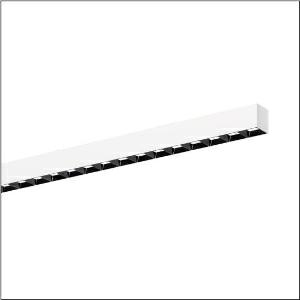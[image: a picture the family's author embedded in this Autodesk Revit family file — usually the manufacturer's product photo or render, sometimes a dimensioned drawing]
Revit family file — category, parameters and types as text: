
# Revit family: silica_r__21_51mx22da34wb_da43
name_source: partatom
category: Lighting Fixtures
units: mm (PartAtom-declared; Revit-internal decimal feet)

## family parameters
Cut with Voids When Loaded = No
Host = Face
Light Source = No
Part Type = Normal
Room Calculation Point = No
Round Connector Dimension = Use Diameter
Shared = No

## types (1)
- --- (1 x LED, 4320 lm, 27.4 W, 3000K)
    Apparent Load = 27 VA
    CIE Flux Codes = 86 100 100 100 100
    Color Rendering = 80
    Color Temperature = 3000K
    Default Elevation = 1800 mm
    Description = Silica® 21, office luminaire, primary light control with darklight reflector, of PMMA, black, CAT 2 (L<= 3000cd/m²), light emission: direct distribution, primary light characteristic: symmetric, installation type: surface-mounted, LED, rated luminous flux: 4.320lm, luminous efficacy: 158lm/W, light colour: 830, colour temperature: 3000K, with terminal, 3+2-pole, max. 2.5mm², mains connection: 220..240V, AC, 50/60Hz, rated input power: 27.4W, luminaire housing, of aluminium, traffic white (RAL 9016), length: 1.204mm, width: 53mm, height: 53mm, protection rating (complete): IP20, insulation class (complete): insulation class I (protective earthing), certification: CE, permissible operating ambient temperature: 0..+35°C, standard: EN 50419, packaging unit: 1 piece
    Height = 0 mm  [stored 0 ft]
    Lamp = 1 x LED
    Lamp Light Flux = 4320 lm
    Lamp Power = 27.4 W
    Lamp count = 1
    Length = 1204 mm
    Luminous efficacy = 158 lm/W
    Manufacturer = Siteco
    ModVariant = No
    Model = 51MX22DA34WB
    Mounting Place = Ceiling
    Mounting Type = Recessed
    Number of Poles = 1
    OnlyDefault = Yes
    Power Factor = 1
    Product Name = Silica® 21
    Product group = office luminaire | ceiling recessed
    ProductGroupID = 400
    Protection Class = Protection class I
    Protection Degree = IP 20
    RLX_Detail_Level = 1
    RLX_Emergency_Light_Flux = 0 lm
    RLX_Emergency_Type = 0
    RLX_Emergency_Type_DB = No
    RlxData = <blob elided: 41201 chars, md5=f2044032>
    Socket = socket
    Standby Power = 0 W
    System Light Flux = 4320 lm
    System Power = 27 W
    Type Comments = factory setting: luminous flux: 100 % | dim-lin: 254 | 392 mA
    Type Image = l_1335873.jpg
    URL = http://relux.com
    VarID = @adj_095267
    Voltage = 0 V
    Weight = 0.00 kg
    Width = 53 mm

note: [stored X ft] marks values corroborated as IEEE doubles in the binary element streams (Revit-internal decimal feet)

## geometry (parser evidence)
native form markers: Blend x4, Sweep x10
no freeform markers — native parametric forms only
